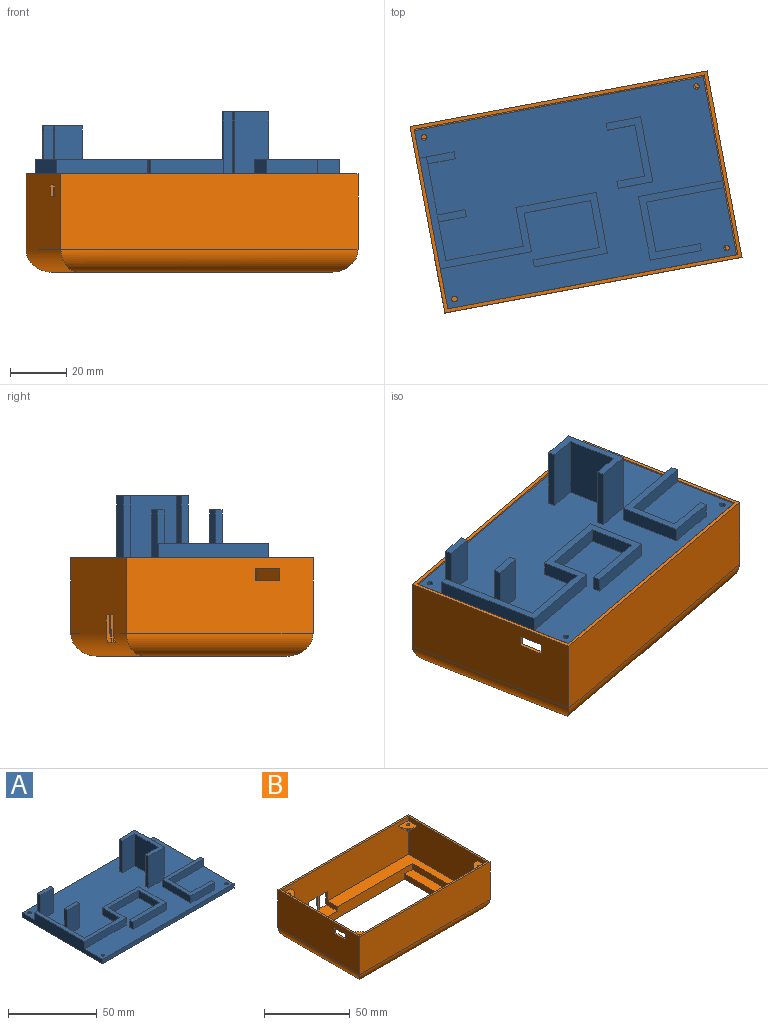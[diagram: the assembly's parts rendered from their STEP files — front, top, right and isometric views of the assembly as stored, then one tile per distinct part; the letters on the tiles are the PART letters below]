
ASSEMBLY  parts=2 mates=1
PART A: 51 faces, bbox 104.5x64.5x25 mm
  f0: plane 104.5x64.5mm, normal (0,0,1), area 6015.2mm2, adj f1,f2,f3,f4,f5,f6,f7,f8
  f1: plane 64.5x8mm, normal (1,0,0), area 206mm2, adj f0,f2,f7,f9,f47,f48,f49
  f2: plane 104.5x3mm, normal (0,1,0), area 313.5mm2, adj f0,f1,f3,f9
  f3: plane 64.5x8mm, normal (-1,0,0), area 393.5mm2, adj f0,f2,f7,f9,f10,f35,f41
  f4: cylinder r=1mm len=3mm, axis (0,0,-1), area 18.8mm2, adj f0,f9
  f5: cylinder r=1mm len=3mm, axis (0,0,-1), area 18.8mm2, adj f0,f9
  f6: cylinder r=1mm len=3mm, axis (0,0,-1), area 18.8mm2, adj f0,f9
  f7: plane 104.5x3mm, normal (0,-1,0), area 313.5mm2, adj f0,f1,f3,f9
  f8: cylinder r=1mm len=3mm, axis (0,0,-1), area 18.8mm2, adj f0,f9
  f9: plane 104.5x64.5mm, normal (0,0,-1), area 6727.7mm2, adj f1,f2,f3,f4,f5,f6,f7,f8
  f10: plane 17x12.5mm, normal (0,1,0), area 182.5mm2, adj f0,f3,f11,f13,f14,f41
  f11: plane 12x2.5mm, normal (-1,0,0), area 30mm2, adj f10,f12,f14,f41
  f12: plane 17x10mm, normal (0,-1,0), area 170mm2, adj f0,f11,f13,f14,f28
  f13: plane 17x2.5mm, normal (1,0,0), area 42.5mm2, adj f0,f10,f12,f14
  f14: plane 10x2.5mm, normal (0,0,1), area 25mm2, adj f10,f11,f12,f13
  f15: plane 17x10mm, normal (0,1,0), area 170mm2, adj f0,f16,f18,f19,f28
  f16: plane 12x2.5mm, normal (-1,0,0), area 30mm2, adj f15,f17,f19,f41
  f17: plane 17x10mm, normal (0,-1,0), area 170mm2, adj f0,f16,f18,f19,f29
  f18: plane 17x2.5mm, normal (1,0,0), area 42.5mm2, adj f0,f15,f17,f19
  f19: plane 10x2.5mm, normal (0,0,1), area 25mm2, adj f15,f16,f17,f18
  f20: plane 22x10mm, normal (0,-1,0), area 220mm2, adj f0,f21,f27,f50
  f21: plane 22x18.5mm, normal (-1,0,0), area 407mm2, adj f0,f20,f22,f50
  f22: plane 22x10mm, normal (0,1,0), area 220mm2, adj f0,f21,f23,f50
  f23: plane 22x2.5mm, normal (-1,0,0), area 55mm2, adj f0,f22,f24,f50
  f24: plane 22x12.5mm, normal (0,-1,0), area 275mm2, adj f0,f23,f25,f50
  f25: plane 23.5x22mm, normal (1,0,0), area 517mm2, adj f0,f24,f26,f50
  f26: plane 22x12.5mm, normal (0,1,0), area 275mm2, adj f0,f25,f27,f50
  f27: plane 22x2.5mm, normal (-1,0,0), area 55mm2, adj f0,f20,f26,f50
  f28: plane 18.5x5mm, normal (1,0,0), area 92.5mm2, adj f0,f12,f15,f41
  f29: plane 14x5mm, normal (1,0,0), area 70mm2, adj f0,f17,f34,f41
  f30: plane 26.5x5mm, normal (0,-1,0), area 132.5mm2, adj f0,f31,f40,f41
  f31: plane 22x5mm, normal (1,0,0), area 110mm2, adj f0,f30,f32,f41
  f32: plane 29x5mm, normal (0,1,0), area 145mm2, adj f0,f31,f33,f41
  f33: plane 14x5mm, normal (-1,0,0), area 70mm2, adj f0,f32,f34,f41
  f34: plane 28x5mm, normal (0,1,0), area 140mm2, adj f0,f29,f33,f41
  f35: plane 33x5mm, normal (0,-1,0), area 165mm2, adj f0,f3,f36,f41
  f36: plane 14x5mm, normal (1,0,0), area 70mm2, adj f0,f35,f37,f41
  f37: plane 24x5mm, normal (0,-1,0), area 120mm2, adj f0,f36,f38,f41
  f38: plane 17x5mm, normal (-1,0,0), area 85mm2, adj f0,f37,f39,f41
  f39: plane 24x5mm, normal (0,1,0), area 120mm2, adj f0,f38,f40,f41
  f40: plane 5x2.5mm, normal (-1,0,0), area 12.5mm2, adj f0,f30,f39,f41
  f41: plane 59.5x45.5mm, normal (0,0,1), area 386.2mm2, adj f3,f10,f11,f16,f28,f29,f30,f31
  f42: plane 23x5mm, normal (-1,0,0), area 115mm2, adj f0,f43,f48,f49
  f43: plane 18.5x5mm, normal (0,-1,0), area 92.5mm2, adj f0,f42,f44,f49
  f44: plane 5x2.5mm, normal (1,0,0), area 12.5mm2, adj f0,f43,f45,f49
  f45: plane 16x5mm, normal (0,1,0), area 80mm2, adj f0,f44,f46,f49
  f46: plane 18x5mm, normal (1,0,0), area 90mm2, adj f0,f45,f47,f49
  f47: plane 28x5mm, normal (0,-1,0), area 140mm2, adj f0,f1,f46,f49
  f48: plane 30.5x5mm, normal (0,1,0), area 152.5mm2, adj f0,f1,f42,f49
  f49: plane 30.5x23mm, normal (0,0,1), area 167.5mm2, adj f1,f42,f43,f44,f45,f46,f47,f48
  f50: plane 23.5x12.5mm, normal (0,0,1), area 108.7mm2, adj f20,f21,f22,f23,f24,f25,f26,f27
PART B: 51 faces, bbox 107.5x67.5x35 mm
  f0: plane 7.5x1.25mm, normal (0,0,-1), area 9.4mm2, adj f2,f7,f25,f48
  f1: plane 65x27mm, normal (1,0,0), area 1655mm2, adj f2,f4,f9,f14,f32,f33,f34,f35
  f2: plane 105x30mm, normal (0,-1,0), area 2679.7mm2, adj f0,f1,f3,f9,f14,f24,f25,f26
  f3: plane 65x27mm, normal (-1,0,0), area 1691mm2, adj f2,f4,f9,f14,f38,f39,f40,f41
  f4: plane 105x27mm, normal (0,1,0), area 2771mm2, adj f1,f3,f9,f14,f36,f37,f38,f39
  f5: plane 67.5x27mm, normal (1,0,0), area 1822.5mm2, adj f7,f13,f14,f21
  f6: plane 67.5x27mm, normal (-1,0,0), area 1786.5mm2, adj f7,f13,f14,f22,f32,f33,f34,f35
  f7: plane 107.5x27mm, normal (0,1,0), area 2801.4mm2, adj f0,f5,f6,f11,f14,f24,f25,f31
  f8: plane 48.2x4.2mm, normal (1,0,0), area 142.4mm2, adj f9,f10,f12,f20,f27,f29,f30
  f9: plane 105x65mm, normal (0,0,1), area 2030mm2, adj f1,f2,f3,f4,f8,f10,f12,f16
  f10: plane 95x8mm, normal (0,-1,0), area 665.6mm2, adj f8,f9,f15,f16,f17,f18,f19,f20
  f11: cylinder r=8mm len=107.5mm, axis (-1,0,0), area 1231.7mm2, adj f7,f15,f21,f22,f24,f25,f26,f50
  f12: plane 95x8mm, normal (0,1,0), area 710.6mm2, adj f8,f9,f15,f16,f17,f18,f19,f20
  f13: plane 107.5x27mm, normal (0,-1,0), area 2902.5mm2, adj f5,f6,f14,f23
  f14: plane 107.5x67.5mm, normal (0,0,1), area 431.3mm2, adj f1,f2,f3,f4,f5,f6,f7,f13
  f15: plane 91.5x51.5mm, normal (0,0,-1), area 759.8mm2, adj f10,f11,f12,f17,f19,f21,f22,f23
  f16: plane 48.2x4.2mm, normal (-1,0,0), area 202.4mm2, adj f9,f10,f12,f18
  f17: plane 48.2x3.8mm, normal (-1,0,0), area 183.2mm2, adj f10,f12,f15,f18
  f18: plane 48.2x6.5mm, normal (0,0,1), area 313.3mm2, adj f10,f12,f16,f17
  f19: plane 48.2x3.8mm, normal (1,0,0), area 183.2mm2, adj f10,f12,f15,f20
  f20: plane 48.2x6.5mm, normal (0,0,1), area 313.3mm2, adj f8,f10,f12,f19
  f21: cylinder r=8mm len=67.5mm, axis (0,1,0), area 775.2mm2, adj f5,f11,f15,f23
  f22: cylinder r=8mm len=67.5mm, axis (0,-1,0), area 775.2mm2, adj f6,f11,f15,f23
  f23: cylinder r=8mm len=107.5mm, axis (1,0,0), area 1277.8mm2, adj f13,f15,f21,f22
  f24: plane 9.74x9.65mm, normal (-1,0,0), area 36.8mm2, adj f2,f7,f9,f10,f11,f26,f31
  f25: plane 9.74x9.65mm, normal (1,0,0), area 36.8mm2, adj f0,f2,f7,f9,f10,f11,f26
  f26: plane 15x9.07mm, normal (0,0,1), area 135.3mm2, adj f2,f10,f11,f24,f25,f48,f49
  f27: plane 4.5x3mm, normal (0,-1,0), area 13.5mm2, adj f8,f9,f28,f30
  f28: plane 20x3mm, normal (1,0,0), area 60mm2, adj f9,f27,f29,f30
  f29: plane 4.5x3mm, normal (0,1,0), area 13.5mm2, adj f8,f9,f28,f30
  f30: plane 20x4.5mm, normal (0,0,1), area 90mm2, adj f8,f27,f28,f29
  f31: plane 6.5x1.25mm, normal (0,0,-1), area 8.1mm2, adj f2,f7,f24,f49
  f32: plane 4x1.25mm, normal (0,-1,0), area 5mm2, adj f1,f6,f33,f35
  f33: plane 9x1.25mm, normal (0,0,1), area 11.3mm2, adj f1,f6,f32,f34
  f34: plane 4x1.25mm, normal (0,1,0), area 5mm2, adj f1,f6,f33,f35
  f35: plane 9x1.25mm, normal (0,0,-1), area 11.3mm2, adj f1,f6,f32,f34
  f36: cone r=0mm half-angle=45deg, axis (0,0,1), area 66.6mm2, adj f1,f4,f37,f46
  f37: plane 8x8mm, normal (0,0,1), area 47.1mm2, adj f1,f4,f36,f46
  f38: cone r=0mm half-angle=45deg, axis (0,0,1), area 66.6mm2, adj f3,f4,f39,f47
  f39: plane 8x8mm, normal (0,0,1), area 47.1mm2, adj f3,f4,f38,f47
  f40: cone r=0mm half-angle=45deg, axis (0,0,1), area 66.6mm2, adj f2,f3,f41,f45
  f41: plane 8x8mm, normal (0,0,1), area 47.1mm2, adj f2,f3,f40,f45
  f42: cone r=0mm half-angle=45deg, axis (0,0,1), area 66.6mm2, adj f1,f2,f43,f44
  f43: plane 8x8mm, normal (0,0,1), area 47.1mm2, adj f1,f2,f42,f44
  f44: cylinder r=1mm len=4.76mm, axis (0,0,1), area 23.2mm2, adj f42,f43
  f45: cylinder r=1mm len=4.76mm, axis (0,0,1), area 23.2mm2, adj f40,f41
  f46: cylinder r=1mm len=4.76mm, axis (0,0,1), area 23.2mm2, adj f36,f37
  f47: cylinder r=1mm len=4.76mm, axis (0,0,1), area 23.2mm2, adj f38,f39
  f48: plane 9.74x1.25mm, normal (-1,0,0), area 9.3mm2, adj f0,f2,f26,f50
  f49: plane 9.74x1.25mm, normal (1,0,0), area 9.3mm2, adj f2,f26,f31,f50
  f50: plane 9.74x1mm, normal (0,1,-0.06), area 9.8mm2, adj f7,f11,f48,f49
PLACE A rot(axis=(0,0,1),10.6deg) t=(-3.27,4.88,37.51)mm
PLACE B rot(axis=(0,0,1),10.6deg) t=(-3.07,5.17,5.51)mm
MATE fastened A.f5 <-> B.f46  axis (0,0,-1) through (-46.29,-32.94,37.51)mm
